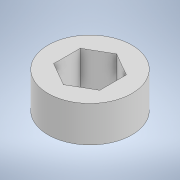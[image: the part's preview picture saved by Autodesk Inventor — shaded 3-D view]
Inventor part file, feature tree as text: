
AUTODESK INVENTOR PART (.ipt)
format: ipt  version: 2022.2 (Build 262287010, 287A)  size: 104,960 bytes
history: native  units: in
note: dims shown in document units (in); Inventor stores cm internally (conversion verified against a paired STEP export)
features: extrude x1, sketch x1
ambient origin geometry x8: Origin, YZ Plane, XZ Plane, XY Plane, X Axis, Y Axis, Z Axis, Center Point
bodies: Solid1 (feature_tree)
feature tree (2):
  extrude  "Extrusion1"  Depth=0.3in
  sketch  "Sketch1"  dims[d0=0.385in d1=0.7in d2=0.3in d3=0.0in]
